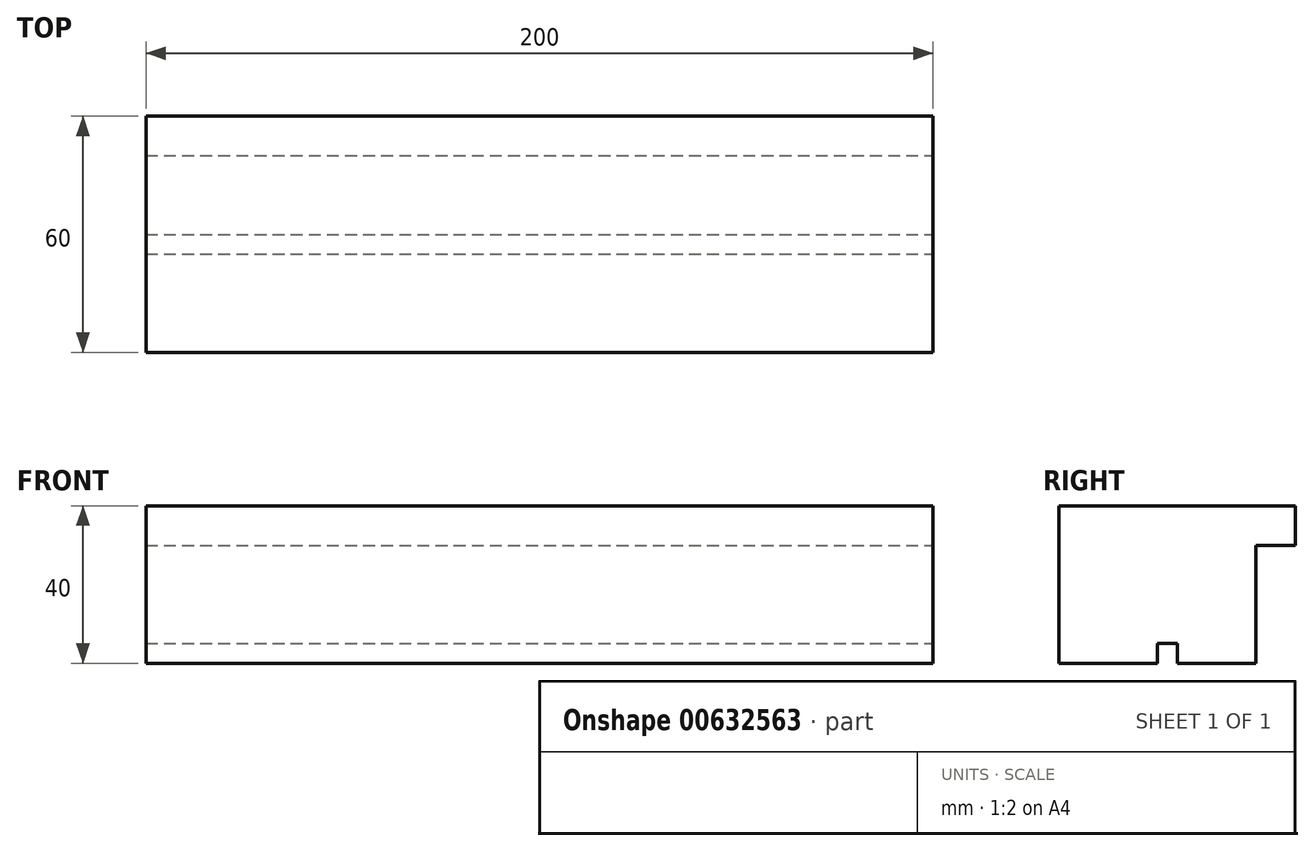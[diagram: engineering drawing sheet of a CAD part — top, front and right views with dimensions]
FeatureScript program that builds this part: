
annotation { "Feature Type Name" : "Feature", "Feature Type Description" : "" }
export const myFeature = defineFeature(function(context is Context, id is Id, definition is map)
    precondition{}
    {
        {
            var Q0;
            Q0=qCreatedBy(makeId("Right.planeOp"),FACE);
            var sketch = newSketch(context, id + "F0", { "sketchPlane" : qUnion([Q0])});
            skLineSegment(sketch, "E0.bottom", {"start": v(10, 40) * mm, "end": v(-50, 40) * mm});
            skLineSegment(sketch, "E0.top", {"start": v(10, 30) * mm, "end": v(0, 30) * mm});
            skLineSegment(sketch, "E0.left", {"start": v(10, 40) * mm, "end": v(10, 30) * mm});
            skLineSegment(sketch, "E0.right", {"start": v(-50, 40) * mm, "end": v(-50, 30) * mm});
            skLineSegment(sketch, "E1.bottom", {"start": v(0, 0) * mm, "end": v(-50, 0) * mm});
            skLineSegment(sketch, "E1.left", {"start": v(0, 0) * mm, "end": v(0, 30) * mm});
            skLineSegment(sketch, "E1.right", {"start": v(-50, 0) * mm, "end": v(-50, 30) * mm});
            skSolve(sketch);
        }
        {
            var Q0;
            Q0=makeQuery(id+"F0.imprint","IMPRINT",FACE,{"disambiguationData":[TD([[makeQuery(id+"F0.imprint","IMPRINT",EDGE,{"derivedFrom":sQuery(id+"F0.wireOp",EDGE,"E0.bottom")}),1.0]])]});
            extrude(context, id + "F1", {"entities" : qUnion([Q0]), "oppositeDirection" : true, "depth" : 200 * mm, "offsetDistance" : 25 * mm});
        }
        {
            var Q0;
            Q0=makeQuery(id+"F1.opExtrude","SWEPT_FACE",FACE,{"disambiguationData":[OSD([sQuery(id+"F0.wireOp",EDGE,"E1.bottom")])]});
            var sketch = newSketch(context, id + "F2", { "sketchPlane" : qUnion([Q0])});
            skLineSegment(sketch, "E2.bottom", {"start": v(-200, 20) * mm, "end": v(0, 20) * mm});
            skLineSegment(sketch, "E2.top", {"start": v(-200, 25) * mm, "end": v(0, 25) * mm});
            skLineSegment(sketch, "E2.left", {"start": v(-200, 20) * mm, "end": v(-200, 25) * mm});
            skLineSegment(sketch, "E2.right", {"start": v(0, 20) * mm, "end": v(0, 25) * mm});
            skSolve(sketch);
        }
        {
            var Q0;
            Q0=makeQuery(id+"F2.imprint","IMPRINT",FACE,{"disambiguationData":[TD([[makeQuery(id+"F2.imprint","IMPRINT",EDGE,{"derivedFrom":sQuery(id+"F2.wireOp",EDGE,"E2.bottom")}),1.0]])]});
            var Q1;
            Q1=sQuery(id+"F2.wireOp",EDGE,"E2.left");
            var Q2;
            Q2=sQuery(id+"F2.wireOp",EDGE,"E2.bottom");
            var Q3;
            Q3=sQuery(id+"F2.wireOp",EDGE,"E2.right");
            var Q4;
            Q4=sQuery(id+"F2.wireOp",EDGE,"E2.top");
            extrude(context, id + "F3", {"entities" : qUnion([Q0]), "operationType" : NewBodyOperationType.REMOVE, "surfaceEntities" : qUnion([Q1, Q2, Q3, Q4]), "oppositeDirection" : true, "depth" : 5 * mm, "offsetDistance" : 25 * mm});
        }
    });
